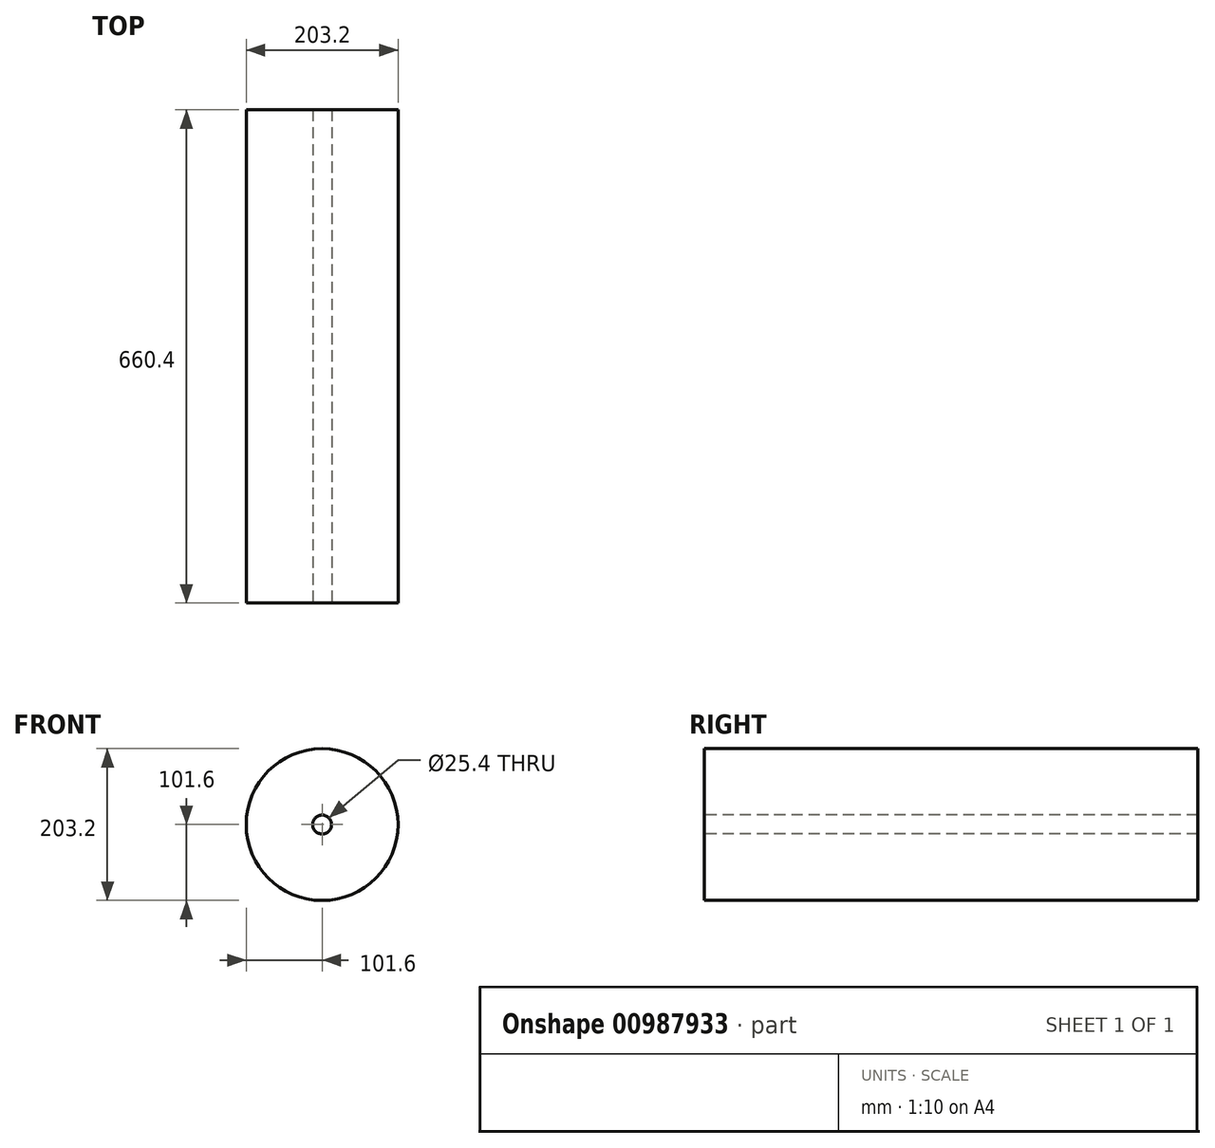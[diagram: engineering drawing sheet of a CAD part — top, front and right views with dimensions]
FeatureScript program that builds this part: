
annotation { "Feature Type Name" : "Feature", "Feature Type Description" : "" }
export const myFeature = defineFeature(function(context is Context, id is Id, definition is map)
    precondition{}
    {
        {
            var Q0;
            Q0=qCreatedBy(makeId("Front.planeOp"),FACE);
            var sketch = newSketch(context, id + "F0", { "sketchPlane" : qUnion([Q0])});
            skCircle(sketch, "E0", {"center": v(0, 0) * mm, "radius": 101.6 * mm});
            skSolve(sketch);
        }
        {
            var Q0;
            Q0=makeQuery(id+"F0.imprint","IMPRINT",FACE,{"disambiguationData":[TD([[makeQuery(id+"F0.imprint","IMPRINT",EDGE,{"derivedFrom":sQuery(id+"F0.wireOp",EDGE,"E0")}),1.0]])]});
            extrude(context, id + "F1", {"entities" : qUnion([Q0]), "depth" : 762 * mm, "offsetDistance" : 25.4 * mm});
        }
        {
            var Q0;
            Q0=makeQuery(id+"F1.opExtrude","CAP_FACE",FACE,{"disambiguationData":[OSD([sQuery(id+"F0.wireOp",EDGE,"E0")])],"isStart":false});
            var sketch = newSketch(context, id + "F2", { "sketchPlane" : qUnion([Q0])});
            skCircle(sketch, "E1", {"center": v(0, 0) * mm, "radius": 12.7 * mm});
            skSolve(sketch);
        }
        {
            var Q0;
            Q0=makeQuery(id+"F2.imprint","IMPRINT",FACE,{"disambiguationData":[TD([[makeQuery(id+"F2.imprint","IMPRINT",EDGE,{"derivedFrom":sQuery(id+"F2.wireOp",EDGE,"E1")}),1.0]])]});
            extrude(context, id + "F3", {"entities" : qUnion([Q0]), "operationType" : NewBodyOperationType.REMOVE, "endBound" : BoundingType.THROUGH_ALL, "oppositeDirection" : true, "depth" : 25.4 * mm, "offsetDistance" : 25.4 * mm});
        }
        {
            var Q0;
            Q0=makeQuery(id+"F1.opExtrude","CAP_FACE",FACE,{"disambiguationData":[OSD([sQuery(id+"F0.wireOp",EDGE,"E0")])],"isStart":false});
            extrude(context, id + "F4", {"entities" : qUnion([Q0]), "operationType" : NewBodyOperationType.REMOVE, "oppositeDirection" : true, "depth" : 101.6 * mm, "offsetDistance" : 25.4 * mm});
        }
    });
